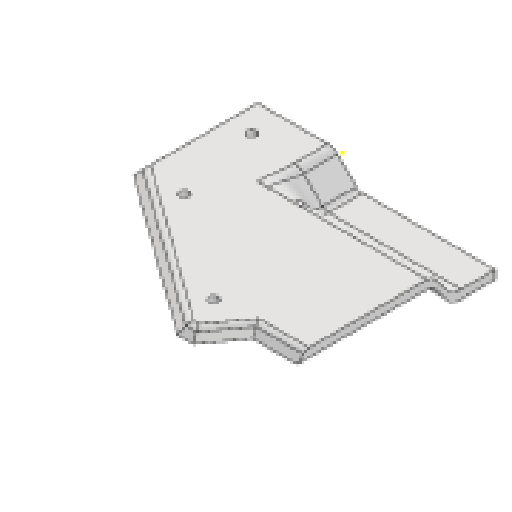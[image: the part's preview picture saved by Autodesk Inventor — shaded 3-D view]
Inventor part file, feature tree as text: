
AUTODESK INVENTOR PART (.ipt)
format: ipt  version: 2025 (Build 290162000, 162)  size: 335,360 bytes
history: native  units: mm
features: other x8, sketch x6, reference x6, extrude x4, projected_geometry x2, plane x1, loft x1, chamfer x1, fillet x1
ambient origin geometry x8: Origin, YZ Plane, XZ Plane, XY Plane, X Axis, Y Axis, Z Axis, Center Point
bodies: Solid1 (feature_tree)
feature tree (30):
  extrude  "Extrusion1"  Depth=20.0mm
  plane  "Work Plane1"
  loft  "Loft1"
  extrude  "Extrusion2"  TaperAngle=0.0deg  [1 undecoded]
  sketch  "Sketch4"  dims[d11=5.0mm d12=2.0mm d13=45.0deg d14=5.5mm d15=10.0mm d16=0.0mm]
  extrude  "Extrusion3"  Depth=10.0mm
  chamfer  "Chamfer1"  Distance=10.0mm
  extrude  "Extrusion4"  [1 undecoded]
  fillet  "Fillet1"  [1 undecoded]
  sketch  "Sketch1"  dims[d0=20.0mm d1=0.0mm d2=20.0mm]
  reference  "Reference1"
  sketch  "Sketch2"  dims[d3=10.0mm d4=90.0deg d5=10.0mm d6=90.0deg]
  projected_geometry  "Projected Loop1"
  other  "Edges1"
  sketch  "Sketch3"  dims[d7=97.0mm d8=0.0mm d9=0.0mm d10=0.0mm]
  projected_geometry  "Projected Loop2"
  sketch  "Sketch5"  dims[d18=5.0mm]
  reference  "Reference2"
  reference  "Reference3"
  reference  "Reference4"
  sketch  "Sketch6"
  reference  "Reference5"
  reference  "Reference6"
  other  "<userpath>\Desktop\puppycat\woodhouseMK1.iam"
  other  "woodhouseMK1.iam"
  other  "middleLeftSidePlate:1"
  other  "rearSkidPlate:1"
  other  "trackBase:2"
  other  "rearStrut:2"
  other  "lowerSkidPlateRear:1"
note: 3 required parameter values undecoded (feature->parameter linkage not recoverable at this tier; creation-order binding heuristic only, values carry confidence <= 0.55)
